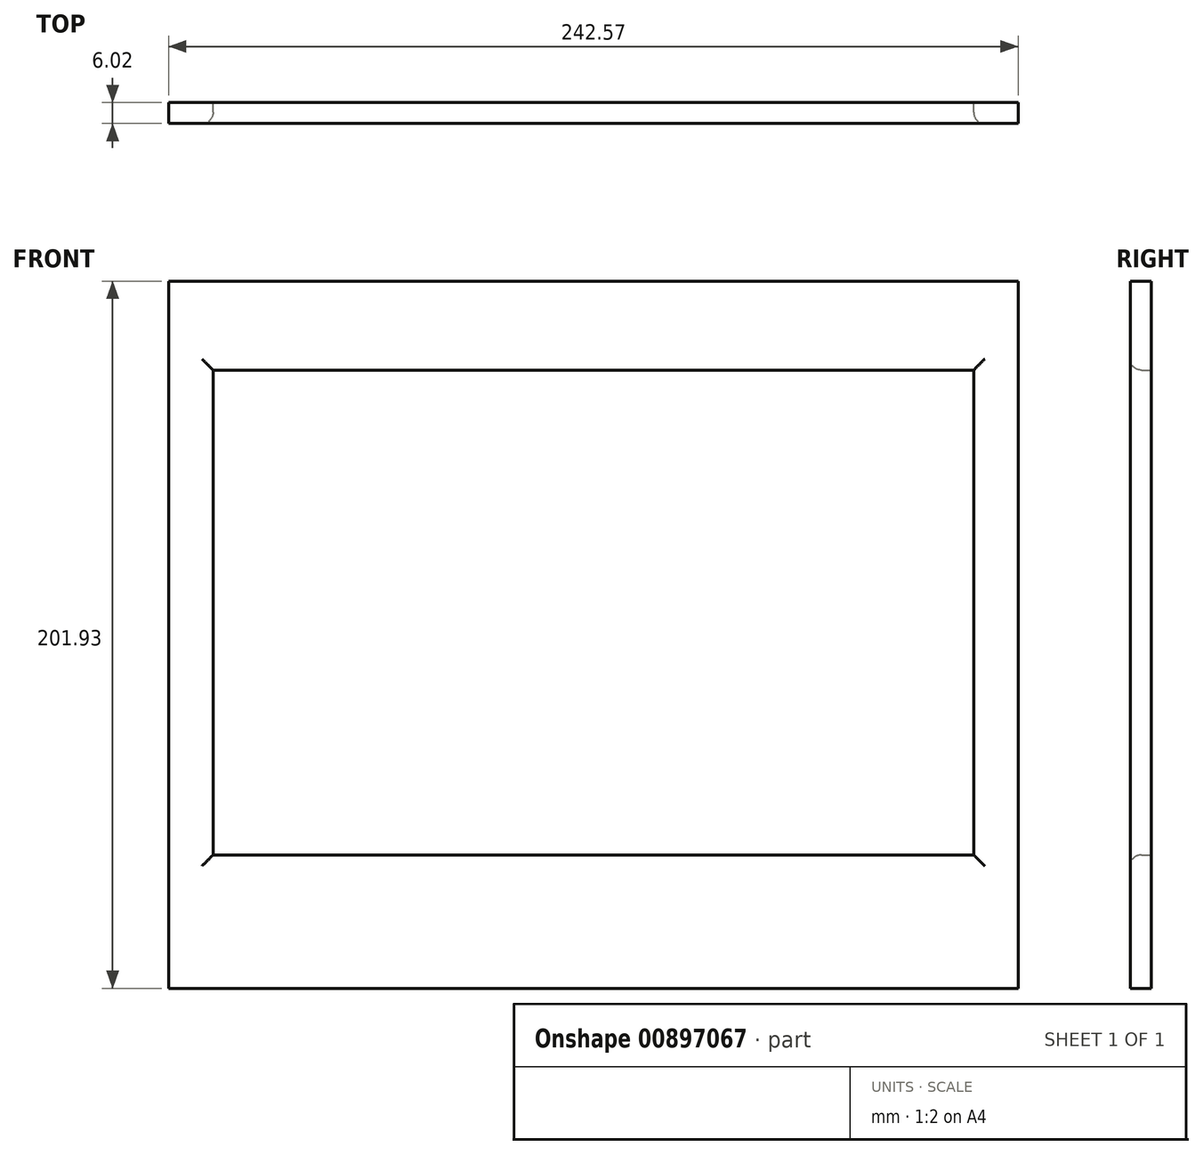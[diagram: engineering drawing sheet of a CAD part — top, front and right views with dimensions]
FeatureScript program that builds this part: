
annotation { "Feature Type Name" : "Feature", "Feature Type Description" : "" }
export const myFeature = defineFeature(function(context is Context, id is Id, definition is map)
    precondition{}
    {
        {
            var Q0;
            Q0=qCreatedBy(makeId("Front.planeOp"),FACE);
            var sketch = newSketch(context, id + "F0", { "sketchPlane" : qUnion([Q0])});
            skLineSegment(sketch, "E0.bottom", {"start": v(0, 0) * mm, "end": v(242.57, 0) * mm});
            skLineSegment(sketch, "E0.top", {"start": v(0, 201.93) * mm, "end": v(242.57, 201.93) * mm});
            skLineSegment(sketch, "E0.left", {"start": v(0, 0) * mm, "end": v(0, 201.93) * mm});
            skLineSegment(sketch, "E0.right", {"start": v(242.57, 0) * mm, "end": v(242.57, 201.93) * mm});
            skLineSegment(sketch, "E1.bottom", {"start": v(12.7, 176.53) * mm, "end": v(229.87, 176.53) * mm});
            skLineSegment(sketch, "E1.top", {"start": v(12.7, 38.1) * mm, "end": v(229.87, 38.1) * mm});
            skLineSegment(sketch, "E1.left", {"start": v(12.7, 176.53) * mm, "end": v(12.7, 38.1) * mm});
            skLineSegment(sketch, "E1.right", {"start": v(229.87, 176.53) * mm, "end": v(229.87, 38.1) * mm});
            skPoint(sketch, "E2", {"position": v(121.28, 201.93) * mm});
            skPoint(sketch, "E3", {"position": v(121.28, 176.53) * mm});
            skSolve(sketch);
        }
        {
            var Q0;
            Q0 = qSketchRegion(id + "F0", true);
            extrude(context, id + "F1", {"entities" : qUnion([Q0]), "depth" : 6.02 * mm, "offsetDistance" : 25.4 * mm});
        }
        {
            var Q0;
            Q0=makeQuery(id+"F1.opExtrude","CAP_EDGE",EDGE,{"disambiguationData":[OSD([sQuery(id+"F0.wireOp",EDGE,"E1.left")])],"isStart":false});
            var Q1;
            Q1=makeQuery(id+"F1.opExtrude","CAP_EDGE",EDGE,{"disambiguationData":[OSD([sQuery(id+"F0.wireOp",EDGE,"E1.bottom")])],"isStart":false});
            var Q2;
            Q2=makeQuery(id+"F1.opExtrude","CAP_EDGE",EDGE,{"disambiguationData":[OSD([sQuery(id+"F0.wireOp",EDGE,"E1.right")])],"isStart":false});
            var Q3;
            Q3=makeQuery(id+"F1.opExtrude","CAP_EDGE",EDGE,{"disambiguationData":[OSD([sQuery(id+"F0.wireOp",EDGE,"E1.top")])],"isStart":false});
            fillet(context, id + "F2", {"entities" : qUnion([Q0, Q1, Q2, Q3]), "radius" : 3.17 * mm, "tangentPropagation" : true, "allowEdgeOverflow" : false});
        }
    });
